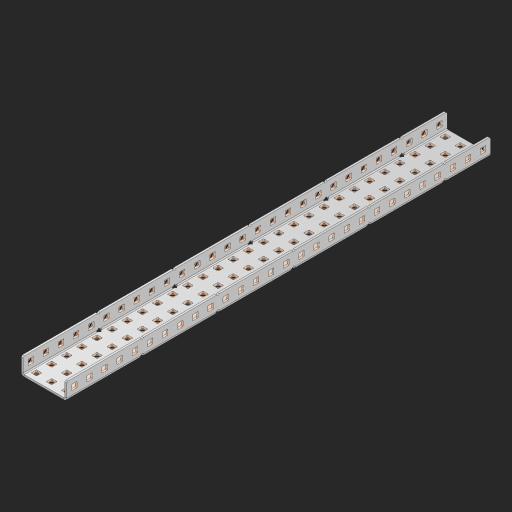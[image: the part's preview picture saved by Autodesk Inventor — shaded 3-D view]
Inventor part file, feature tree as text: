
AUTODESK INVENTOR PART (.ipt)
format: ipt  version: 2023 (Build 270158000, 158)  size: 1,736,704 bytes
history: native  units: in
note: dims shown in document units (in); Inventor stores cm internally (conversion verified against a paired STEP export)
features: other x145, extrude x139, sheet_metal_op x10, sketch x8, mirror x1, pattern_linear x1, chamfer x1
ambient origin geometry x8: Origin, YZ Plane, XZ Plane, XY Plane, X Axis, Y Axis, Z Axis, Center Point
bodies: Solid1 (feature_tree), Body (feature_tree)
feature tree (305):
  other  "Flange Pattern Plane"
  sheet_metal_op  "Flange Pattern"
  sheet_metal_op  "Body Pattern"
  other  "Arc Length"
  mirror  "Notch Mirror"
  pattern_linear  "Notch Pattern"  Spacing1=0.25in  [1 undecoded]
  chamfer  "End Chamfer"
  extrude  "Half Cut"  Depth=0.0625in
  sketch  "Sketch1"  dims[d0=1.5in]
  other  "Plate1"
  sketch  "Sketch2"  dims[d1=14.0in]
  other  "Plate2"
  sheet_metal_op  "Bend1"
  sheet_metal_op  "Corner1"
  sketch  "Sketch3"  dims[d2=0.0625in]
  other  "Flange Pattern Sketch"
  sketch  "Sketch7"  dims[d3=0.0625in]
  other  "Srf1"
  other  "Srf2"
  sketch  "Sketch8"  dims[d4=0.0312in]
  sketch  "Sketch9"  dims[d5=0.125in]
  other  "Srf91"
  sheet_metal_op  "Body Pattern Sketch"
  other  "Srf92"
  sketch  "Sketch13"  dims[d6=0.0625in]
  sketch  "Sketch14"  dims[d7=0.5in d8=90.0deg d9=0.0312in d10=0.25in d11=0.0625in d12=0.0625in d16=0.182in d17=0.02in d18=0.0625in d19=0.0in d20=0.25in d21=0.25in d46=0.172in d47=1.0in d48=0.0in d49=0.182in d50=0.02in d51=0.25in d52=0.25in d53=0.0625in d54=0.0in d55=0.172in d56=1.0in d57=0.0in d60=11.0236in d62=0.5in d63=1.1811in d65=0.5in d85=0.1473in d86=0.1782in d88=0.04in d89=0.0625in d90=0.0in d91=0.04in d92=0.0491in d95=2.5in d96=0.04in d97=0.25in d98=45.0deg d101=0.0in d102=2.497in d131=1.5in d132=11.0236in d134=0.5in d139=0.5in]
  other  "Srf856"
  other  "Srf1310"
  other  "Srf1311"
  other  "Srf1312"
  other  "Srf1376"
  other  "Srf1377"
  other  "Srf1728"
  other  "Srf1755"
  other  "Srf1878"
  other  "Srf1879"
  other  "Srf1880"
  other  "Srf1881"
  other  "Srf1882"
  other  "Srf1883"
  other  "Srf1884"
  other  "Srf1885"
  other  "Srf1886"
  other  "Srf1887"
  other  "Srf1888"
  other  "Srf1889"
  other  "Srf1890"
  other  "Srf1891"
  other  "Srf1892"
  other  "Srf1893"
  other  "Srf1894"
  other  "Srf1895"
  other  "Srf1896"
  other  "Srf1897"
  other  "Srf1898"
  other  "Srf1899"
  other  "Srf1900"
  other  "Srf1901"
  other  "Srf1902"
  other  "Srf1903"
  other  "Srf1904"
  other  "Srf1905"
  other  "Srf1906"
  other  "Srf1907"
  other  "Srf1908"
  other  "Srf1909"
  other  "Srf1910"
  other  "Srf1911"
  other  "Srf1912"
  other  "Srf1913"
  other  "Srf1914"
  other  "Srf1915"
  other  "Srf1916"
  other  "Srf1917"
  other  "Srf1918"
  other  "Srf1919"
  other  "Srf1920"
  other  "Srf1921"
  other  "Srf1922"
  other  "Srf1923"
  other  "Srf1924"
  other  "Srf1925"
  other  "Srf1926"
  other  "Srf1927"
  other  "Srf1942"
  other  "Srf1943"
  other  "Srf1944"
  other  "Srf1945"
  other  "Srf1946"
  other  "Srf1947"
  other  "Srf1948"
  other  "Srf1949"
  other  "Srf1950"
  other  "Srf1951"
  other  "Srf1952"
  other  "Srf1953"
  other  "Srf1954"
  other  "Srf1955"
  other  "Srf1956"
  other  "Srf1957"
  other  "Srf1958"
  other  "Srf1959"
  other  "Srf1960"
  other  "Srf1961"
  other  "Srf1962"
  other  "Srf1963"
  other  "Srf1964"
  other  "Srf1965"
  other  "Srf1966"
  other  "Srf1967"
  other  "Srf1968"
  other  "Srf1969"
  other  "Srf1970"
  other  "Srf1971"
  other  "Srf1972"
  other  "Srf1973"
  other  "Srf1974"
  other  "Srf1975"
  other  "Srf1976"
  other  "Srf1977"
  other  "Srf1978"
  other  "Srf1979"
  other  "Srf1980"
  other  "Srf1981"
  other  "Srf1982"
  other  "Srf1983"
  other  "Srf1984"
  other  "Srf1985"
  other  "Srf1986"
  other  "Srf1987"
  other  "Srf1988"
  other  "Srf1989"
  other  "Srf1990"
  other  "Srf1991"
  other  "Srf1992"
  other  "Srf1993"
  other  "Srf1994"
  other  "Srf1995"
  other  "Srf1996"
  other  "Srf1997"
  other  "Srf1998"
  other  "Srf1999"
  other  "Srf2000"
  other  "Srf2001"
  other  "Srf2002"
  other  "Srf2003"
  other  "Srf2004"
  other  "Srf2005"
  other  "Srf2006"
  other  "Srf2007"
  other  "Srf2008"
  other  "Srf2009"
  other  "Srf2010"
  other  "Srf2011"
  other  "Srf2012"
  other  "Srf2013"
  other  "Srf2014"
  other  "Srf2015"
  other  "Srf2016"
  other  "Srf2017"
  other  "Srf2018"
  other  "Srf2019"
  sheet_metal_op  "Flange Stamp"
  sheet_metal_op  "Flange Circle"
  sheet_metal_op  "Body Stamp"
  sheet_metal_op  "Body Circle"
  sheet_metal_op  "Notch"
  extrude  "ExtrusionSrf2"  Depth=0.0625in
  extrude  "ExtrusionSrf92"  Depth=1.5in
  extrude  "ExtrusionSrf856"  Depth=0.02in
  extrude  "ExtrusionSrf1310"  Depth=0.0625in
  extrude  "ExtrusionSrf1311"  TaperAngle=0.0deg  [1 undecoded]
  extrude  "ExtrusionSrf1312"  Depth=0.25in
  extrude  "ExtrusionSrf1376"  Depth=0.25in
  extrude  "ExtrusionSrf1377"  Depth=1.5in
  extrude  "ExtrusionSrf1728"  Depth=1.5in TaperAngle=0.0deg
  extrude  "ExtrusionSrf1755"  Depth=1.5in
  extrude  "ExtrusionSrf1878"  Depth=0.02in
  extrude  "ExtrusionSrf1879"  Depth=0.25in
  extrude  "ExtrusionSrf1880"  Depth=0.25in
  extrude  "ExtrusionSrf1881"  Depth=0.0625in
  extrude  "ExtrusionSrf1882"  TaperAngle=0.0deg  [1 undecoded]
  extrude  "ExtrusionSrf1883"  Depth=1.5in
  extrude  "ExtrusionSrf1884"  Depth=1.5in TaperAngle=0.0deg
  extrude  "ExtrusionSrf1885"  Depth=1.5in
  extrude  "ExtrusionSrf1886"  Depth=1.5in
  extrude  "ExtrusionSrf1887"  Depth=1.5in
  extrude  "ExtrusionSrf1888"  Depth=1.5in
  extrude  "ExtrusionSrf1889"  Depth=1.5in
  extrude  "ExtrusionSrf1890"  Depth=0.0625in
  extrude  "ExtrusionSrf1891"  TaperAngle=0.0deg  [1 undecoded]
  extrude  "ExtrusionSrf1892"  Depth=1.5in
  extrude  "ExtrusionSrf1893"  Depth=1.5in
  extrude  "ExtrusionSrf1894"  Depth=1.5in
  extrude  "ExtrusionSrf1895"  Depth=0.25in TaperAngle=45.0deg
  extrude  "ExtrusionSrf1896"  TaperAngle=0.0deg  [1 undecoded]
  extrude  "ExtrusionSrf1897"  Depth=1.5in
  extrude  "ExtrusionSrf1898"  Depth=1.5in
  extrude  "ExtrusionSrf1899"  Depth=1.5in
  extrude  "ExtrusionSrf1900"  Depth=1.5in
  extrude  "ExtrusionSrf1901"  Depth=1.5in
  extrude  "ExtrusionSrf1902"  [1 undecoded]
  extrude  "ExtrusionSrf1903"  [1 undecoded]
  extrude  "ExtrusionSrf1904"  [1 undecoded]
  extrude  "ExtrusionSrf1905"  [1 undecoded]
  extrude  "ExtrusionSrf1906"  [1 undecoded]
  extrude  "ExtrusionSrf1907"  [1 undecoded]
  extrude  "ExtrusionSrf1908"  [1 undecoded]
  extrude  "ExtrusionSrf1909"  [1 undecoded]
  extrude  "ExtrusionSrf1910"  [1 undecoded]
  extrude  "ExtrusionSrf1911"  [1 undecoded]
  extrude  "ExtrusionSrf1912"  [1 undecoded]
  extrude  "ExtrusionSrf1913"  [1 undecoded]
  extrude  "ExtrusionSrf1914"  [1 undecoded]
  extrude  "ExtrusionSrf1915"  [1 undecoded]
  extrude  "ExtrusionSrf1916"  [1 undecoded]
  extrude  "ExtrusionSrf1917"  [1 undecoded]
  extrude  "ExtrusionSrf1918"  [1 undecoded]
  extrude  "ExtrusionSrf1919"  [1 undecoded]
  extrude  "ExtrusionSrf1920"  [1 undecoded]
  extrude  "ExtrusionSrf1921"  [1 undecoded]
  extrude  "ExtrusionSrf1922"  [1 undecoded]
  extrude  "ExtrusionSrf1923"  [1 undecoded]
  extrude  "ExtrusionSrf1924"  [1 undecoded]
  extrude  "ExtrusionSrf1925"  [1 undecoded]
  extrude  "ExtrusionSrf1926"  [1 undecoded]
  extrude  "ExtrusionSrf1927"  [1 undecoded]
  extrude  "ExtrusionSrf1942"  [1 undecoded]
  extrude  "ExtrusionSrf1943"  [1 undecoded]
  extrude  "ExtrusionSrf1944"  [1 undecoded]
  extrude  "ExtrusionSrf1945"  [1 undecoded]
  extrude  "ExtrusionSrf1946"  [1 undecoded]
  extrude  "ExtrusionSrf1947"  [1 undecoded]
  extrude  "ExtrusionSrf1948"  [1 undecoded]
  extrude  "ExtrusionSrf1949"  [1 undecoded]
  extrude  "ExtrusionSrf1950"  [1 undecoded]
  extrude  "ExtrusionSrf1951"  [1 undecoded]
  extrude  "ExtrusionSrf1952"  [1 undecoded]
  extrude  "ExtrusionSrf1953"  [1 undecoded]
  extrude  "ExtrusionSrf1954"  [1 undecoded]
  extrude  "ExtrusionSrf1955"  [1 undecoded]
  extrude  "ExtrusionSrf1956"  [1 undecoded]
  extrude  "ExtrusionSrf1957"  [1 undecoded]
  extrude  "ExtrusionSrf1958"  [1 undecoded]
  extrude  "ExtrusionSrf1959"  [1 undecoded]
  extrude  "ExtrusionSrf1960"  [1 undecoded]
  extrude  "ExtrusionSrf1961"  [1 undecoded]
  extrude  "ExtrusionSrf1962"  [1 undecoded]
  extrude  "ExtrusionSrf1963"  [1 undecoded]
  extrude  "ExtrusionSrf1964"  [1 undecoded]
  extrude  "ExtrusionSrf1965"  [1 undecoded]
  extrude  "ExtrusionSrf1966"  [1 undecoded]
  extrude  "ExtrusionSrf1967"  [1 undecoded]
  extrude  "ExtrusionSrf1968"  [1 undecoded]
  extrude  "ExtrusionSrf1969"  [1 undecoded]
  extrude  "ExtrusionSrf1970"  [1 undecoded]
  extrude  "ExtrusionSrf1971"  [1 undecoded]
  extrude  "ExtrusionSrf1972"  [1 undecoded]
  extrude  "ExtrusionSrf1973"  [1 undecoded]
  extrude  "ExtrusionSrf1974"  [1 undecoded]
  extrude  "ExtrusionSrf1975"  [1 undecoded]
  extrude  "ExtrusionSrf1976"  [1 undecoded]
  extrude  "ExtrusionSrf1977"  [1 undecoded]
  extrude  "ExtrusionSrf1978"  [1 undecoded]
  extrude  "ExtrusionSrf1979"  [1 undecoded]
  extrude  "ExtrusionSrf1980"  [1 undecoded]
  extrude  "ExtrusionSrf1981"  [1 undecoded]
  extrude  "ExtrusionSrf1982"  [1 undecoded]
  extrude  "ExtrusionSrf1983"  [1 undecoded]
  extrude  "ExtrusionSrf1984"  [1 undecoded]
  extrude  "ExtrusionSrf1985"  [1 undecoded]
  extrude  "ExtrusionSrf1986"  [1 undecoded]
  extrude  "ExtrusionSrf1987"  [1 undecoded]
  extrude  "ExtrusionSrf1988"  [1 undecoded]
  extrude  "ExtrusionSrf1989"  [1 undecoded]
  extrude  "ExtrusionSrf1990"  [1 undecoded]
  extrude  "ExtrusionSrf1991"  [1 undecoded]
  extrude  "ExtrusionSrf1992"  [1 undecoded]
  extrude  "ExtrusionSrf1993"  [1 undecoded]
  extrude  "ExtrusionSrf1994"  [1 undecoded]
  extrude  "ExtrusionSrf1995"  [1 undecoded]
  extrude  "ExtrusionSrf1996"  [1 undecoded]
  extrude  "ExtrusionSrf1997"  [1 undecoded]
  extrude  "ExtrusionSrf1998"  [1 undecoded]
  extrude  "ExtrusionSrf1999"  [1 undecoded]
  extrude  "ExtrusionSrf2000"  [1 undecoded]
  extrude  "ExtrusionSrf2001"  [1 undecoded]
  extrude  "ExtrusionSrf2002"  [1 undecoded]
  extrude  "ExtrusionSrf2003"  [1 undecoded]
  extrude  "ExtrusionSrf2004"  [1 undecoded]
  extrude  "ExtrusionSrf2005"  [1 undecoded]
  extrude  "ExtrusionSrf2006"  [1 undecoded]
  extrude  "ExtrusionSrf2007"  [1 undecoded]
  extrude  "ExtrusionSrf2008"  [1 undecoded]
  extrude  "ExtrusionSrf2009"  [1 undecoded]
  extrude  "ExtrusionSrf2010"  [1 undecoded]
  extrude  "ExtrusionSrf2011"  [1 undecoded]
  extrude  "ExtrusionSrf2012"  [1 undecoded]
  extrude  "ExtrusionSrf2013"  [1 undecoded]
  extrude  "ExtrusionSrf2014"  [1 undecoded]
  extrude  "ExtrusionSrf2015"  [1 undecoded]
  extrude  "ExtrusionSrf2016"  [1 undecoded]
  extrude  "ExtrusionSrf2017"  [1 undecoded]
  extrude  "ExtrusionSrf2018"  [1 undecoded]
  extrude  "ExtrusionSrf2019"  [1 undecoded]
note: 109 required parameter values undecoded (feature->parameter linkage not recoverable at this tier; creation-order binding heuristic only, values carry confidence <= 0.55)
